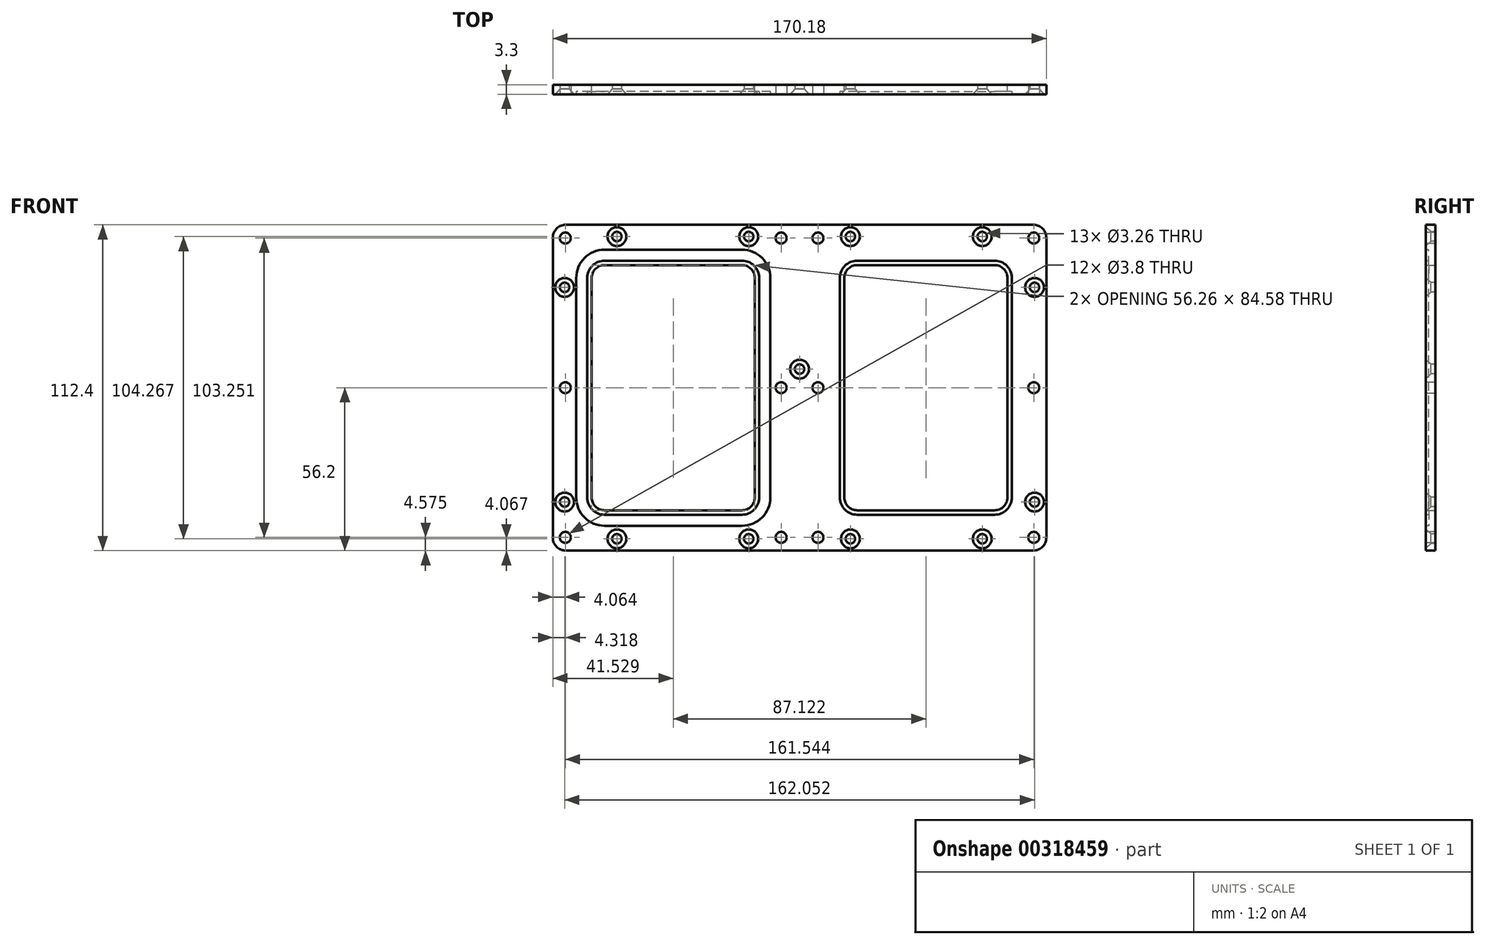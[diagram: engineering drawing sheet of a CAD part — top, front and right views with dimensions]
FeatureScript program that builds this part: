
annotation { "Feature Type Name" : "Feature", "Feature Type Description" : "" }
export const myFeature = defineFeature(function(context is Context, id is Id, definition is map)
    precondition{}
    {
        {
            var Q0;
            Q0=qCreatedBy(makeId("Front.planeOp"),FACE);
            var sketch = newSketch(context, id + "F0", { "sketchPlane" : qUnion([Q0])});
            skLineSegment(sketch, "E0.bottom", {"start": v(-80.64, -56.2) * mm, "end": v(80.65, -56.2) * mm});
            skLineSegment(sketch, "E0.top", {"start": v(-80.64, 56.2) * mm, "end": v(80.64, 56.2) * mm});
            skLineSegment(sketch, "E0.left", {"start": v(-85.1, -51.75) * mm, "end": v(-85.1, 51.75) * mm});
            skLineSegment(sketch, "E0.right", {"start": v(85.1, -51.75) * mm, "end": v(85.09, 51.75) * mm});
            skPoint(sketch, "E0.middle", {"position": v(0, 0) * mm});
            skPoint(sketch, "E1.visualSharp", {"position": v(-85.1, 56.2) * mm});
            skArc(sketch, "E1.filletArc", {"start": v(-80.65, 56.2) * mm, "mid": v(-83.79, 54.9) * mm, "end": v(-85.1, 51.75) * mm});
            skPoint(sketch, "E2.visualSharp", {"position": v(85.09, 56.2) * mm});
            skArc(sketch, "E2.filletArc", {"start": v(85.09, 51.75) * mm, "mid": v(83.79, 54.9) * mm, "end": v(80.64, 56.2) * mm});
            skPoint(sketch, "E3.visualSharp", {"position": v(85.1, -56.2) * mm});
            skArc(sketch, "E3.filletArc", {"start": v(80.65, -56.2) * mm, "mid": v(83.79, -54.9) * mm, "end": v(85.1, -51.75) * mm});
            skPoint(sketch, "E4.visualSharp", {"position": v(-85.1, -56.2) * mm});
            skArc(sketch, "E4.filletArc", {"start": v(-85.1, -51.75) * mm, "mid": v(-83.79, -54.9) * mm, "end": v(-80.64, -56.2) * mm});
            skLineSegment(sketch, "E5.bottom", {"start": v(-19.88, -42.3) * mm, "end": v(-67.25, -42.3) * mm});
            skLineSegment(sketch, "E5.top", {"start": v(-19.88, 42.3) * mm, "end": v(-67.25, 42.3) * mm});
            skLineSegment(sketch, "E5.left", {"start": v(-15.43, -37.85) * mm, "end": v(-15.43, 37.85) * mm});
            skLineSegment(sketch, "E5.right", {"start": v(-71.7, -37.85) * mm, "end": v(-71.7, 37.85) * mm});
            skPoint(sketch, "E5.middle", {"position": v(-43.56, 0) * mm});
            skPoint(sketch, "E6.visualSharp", {"position": v(-71.7, 42.3) * mm});
            skArc(sketch, "E6.filletArc", {"start": v(-67.25, 42.3) * mm, "mid": v(-70.39, 40.99) * mm, "end": v(-71.7, 37.85) * mm});
            skPoint(sketch, "E7.visualSharp", {"position": v(-15.43, 42.3) * mm});
            skArc(sketch, "E7.filletArc", {"start": v(-15.43, 37.85) * mm, "mid": v(-16.73, 40.99) * mm, "end": v(-19.88, 42.3) * mm});
            skPoint(sketch, "E8.visualSharp", {"position": v(-15.43, -42.3) * mm});
            skArc(sketch, "E8.filletArc", {"start": v(-19.88, -42.3) * mm, "mid": v(-16.73, -40.99) * mm, "end": v(-15.43, -37.85) * mm});
            skPoint(sketch, "E9.visualSharp", {"position": v(-71.7, -42.3) * mm});
            skArc(sketch, "E9.filletArc", {"start": v(-71.7, -37.85) * mm, "mid": v(-70.39, -40.99) * mm, "end": v(-67.25, -42.3) * mm});
            skArc(sketch, "E10.MirrorCS", {"start": v(67.25, 42.3) * mm, "mid": v(70.39, 40.99) * mm, "end": v(71.7, 37.85) * mm});
            skArc(sketch, "E11.MirrorCS", {"start": v(15.43, 37.85) * mm, "mid": v(16.73, 40.99) * mm, "end": v(19.88, 42.3) * mm});
            skArc(sketch, "E12.MirrorCS", {"start": v(19.88, -42.3) * mm, "mid": v(16.73, -40.99) * mm, "end": v(15.43, -37.85) * mm});
            skArc(sketch, "E13.MirrorCS", {"start": v(71.7, -37.85) * mm, "mid": v(70.39, -40.99) * mm, "end": v(67.25, -42.3) * mm});
            skPoint(sketch, "E14.MirrorP", {"position": v(43.56, 0) * mm});
            skPoint(sketch, "E15.MirrorP", {"position": v(15.43, -42.3) * mm});
            skLineSegment(sketch, "E16.MirrorCS", {"start": v(71.7, -37.85) * mm, "end": v(71.7, 37.85) * mm});
            skPoint(sketch, "E17.MirrorP", {"position": v(15.43, 42.3) * mm});
            skPoint(sketch, "E18.MirrorP", {"position": v(71.7, 42.3) * mm});
            skPoint(sketch, "E19.MirrorP", {"position": v(71.7, -42.3) * mm});
            skLineSegment(sketch, "E20.MirrorCS", {"start": v(15.43, -37.85) * mm, "end": v(15.43, 37.85) * mm});
            skLineSegment(sketch, "E21.MirrorCS", {"start": v(19.88, 42.3) * mm, "end": v(67.25, 42.3) * mm});
            skLineSegment(sketch, "E22.MirrorCS", {"start": v(19.88, -42.3) * mm, "end": v(67.25, -42.3) * mm});
            skSolve(sketch);
        }
        {
            var Q0;
            Q0=makeQuery(id+"F0.imprint","IMPRINT",FACE,{"disambiguationData":[TD([[makeQuery(id+"F0.imprint","IMPRINT",EDGE,{"derivedFrom":sQuery(id+"F0.wireOp",EDGE,"E0.bottom")}),1.0]])]});
            extrude(context, id + "F1", {"entities" : qUnion([Q0]), "depth" : 3.3 * mm});
        }
        {
            var Q0;
            Q0=makeQuery(id+"F1.opExtrude","CAP_FACE",FACE,{"disambiguationData":[OSD([sQuery(id+"F0.wireOp",EDGE,"E0.bottom"),sQuery(id+"F0.wireOp",EDGE,"E0.top"),sQuery(id+"F0.wireOp",EDGE,"E0.left"),sQuery(id+"F0.wireOp",EDGE,"E0.right"),sQuery(id+"F0.wireOp",EDGE,"E1.filletArc"),sQuery(id+"F0.wireOp",EDGE,"E2.filletArc"),sQuery(id+"F0.wireOp",EDGE,"E3.filletArc"),sQuery(id+"F0.wireOp",EDGE,"E4.filletArc"),sQuery(id+"F0.wireOp",EDGE,"E5.bottom"),sQuery(id+"F0.wireOp",EDGE,"E5.top"),sQuery(id+"F0.wireOp",EDGE,"E5.left"),sQuery(id+"F0.wireOp",EDGE,"E5.right"),sQuery(id+"F0.wireOp",EDGE,"E6.filletArc"),sQuery(id+"F0.wireOp",EDGE,"E7.filletArc"),sQuery(id+"F0.wireOp",EDGE,"E8.filletArc"),sQuery(id+"F0.wireOp",EDGE,"E9.filletArc"),sQuery(id+"F0.wireOp",EDGE,"E10.MirrorCS"),sQuery(id+"F0.wireOp",EDGE,"E11.MirrorCS"),sQuery(id+"F0.wireOp",EDGE,"E12.MirrorCS"),sQuery(id+"F0.wireOp",EDGE,"E13.MirrorCS"),sQuery(id+"F0.wireOp",EDGE,"E16.MirrorCS"),sQuery(id+"F0.wireOp",EDGE,"E20.MirrorCS"),sQuery(id+"F0.wireOp",EDGE,"E21.MirrorCS"),sQuery(id+"F0.wireOp",EDGE,"E22.MirrorCS")])],"isStart":false});
            var sketch = newSketch(context, id + "F2", { "sketchPlane" : qUnion([Q0])});
            skArc(sketch, "E23.0", {"start": v(-13.9, 37.85) * mm, "mid": v(-15.65, 42.07) * mm, "end": v(-19.88, 43.82) * mm});
            skLineSegment(sketch, "E23.1", {"start": v(-13.9, -37.85) * mm, "end": v(-13.9, 37.85) * mm});
            skLineSegment(sketch, "E23.2", {"start": v(-19.88, 43.82) * mm, "end": v(-67.25, 43.82) * mm});
            skArc(sketch, "E23.3", {"start": v(-19.88, -43.82) * mm, "mid": v(-15.65, -42.07) * mm, "end": v(-13.9, -37.85) * mm});
            skArc(sketch, "E23.4", {"start": v(-67.25, 43.81) * mm, "mid": v(-71.47, 42.07) * mm, "end": v(-73.22, 37.85) * mm});
            skLineSegment(sketch, "E23.5", {"start": v(-73.22, -37.85) * mm, "end": v(-73.22, 37.85) * mm});
            skArc(sketch, "E23.6", {"start": v(-73.22, -37.85) * mm, "mid": v(-71.47, -42.07) * mm, "end": v(-67.25, -43.81) * mm});
            skLineSegment(sketch, "E23.7", {"start": v(-19.88, -43.82) * mm, "end": v(-67.25, -43.81) * mm});
            skLineSegment(sketch, "E24.0", {"start": v(-19.88, 47.63) * mm, "end": v(-67.25, 47.63) * mm});
            skArc(sketch, "E24.1", {"start": v(-10.1, 37.85) * mm, "mid": v(-12.96, 44.76) * mm, "end": v(-19.88, 47.63) * mm});
            skArc(sketch, "E24.2", {"start": v(-67.25, 47.62) * mm, "mid": v(-74.16, 44.76) * mm, "end": v(-77.03, 37.85) * mm});
            skLineSegment(sketch, "E24.3", {"start": v(-10.1, -37.85) * mm, "end": v(-10.1, 37.85) * mm});
            skLineSegment(sketch, "E24.4", {"start": v(-77.03, -37.85) * mm, "end": v(-77.03, 37.85) * mm});
            skArc(sketch, "E24.5", {"start": v(-77.03, -37.85) * mm, "mid": v(-74.16, -44.76) * mm, "end": v(-67.25, -47.62) * mm});
            skLineSegment(sketch, "E24.6", {"start": v(-19.88, -47.63) * mm, "end": v(-67.25, -47.62) * mm});
            skArc(sketch, "E24.7", {"start": v(-19.88, -47.63) * mm, "mid": v(-12.96, -44.76) * mm, "end": v(-10.1, -37.85) * mm});
            skArc(sketch, "E25.MirrorCS", {"start": v(73.22, -37.85) * mm, "mid": v(71.47, -42.07) * mm, "end": v(67.25, -43.81) * mm});
            skLineSegment(sketch, "E26.MirrorCS", {"start": v(73.22, -37.85) * mm, "end": v(73.22, 37.85) * mm});
            skArc(sketch, "E27.MirrorCS", {"start": v(67.25, 43.81) * mm, "mid": v(71.47, 42.07) * mm, "end": v(73.22, 37.85) * mm});
            skArc(sketch, "E28.MirrorCS", {"start": v(19.88, -43.82) * mm, "mid": v(15.65, -42.07) * mm, "end": v(13.9, -37.85) * mm});
            skLineSegment(sketch, "E29.MirrorCS", {"start": v(19.88, 43.82) * mm, "end": v(67.25, 43.82) * mm});
            skLineSegment(sketch, "E30.MirrorCS", {"start": v(13.9, -37.85) * mm, "end": v(13.9, 37.85) * mm});
            skArc(sketch, "E31.MirrorCS", {"start": v(13.9, 37.85) * mm, "mid": v(15.65, 42.07) * mm, "end": v(19.88, 43.82) * mm});
            skArc(sketch, "E32.MirrorCS", {"start": v(19.88, -47.63) * mm, "mid": v(12.96, -44.76) * mm, "end": v(10.1, -37.85) * mm});
            skLineSegment(sketch, "E33.MirrorCS", {"start": v(19.88, -47.63) * mm, "end": v(67.25, -47.62) * mm});
            skLineSegment(sketch, "E34.MirrorCS", {"start": v(19.88, -43.82) * mm, "end": v(67.25, -43.81) * mm});
            skArc(sketch, "E35.MirrorCS", {"start": v(77.03, -37.85) * mm, "mid": v(74.16, -44.76) * mm, "end": v(67.25, -47.62) * mm});
            skLineSegment(sketch, "E36.MirrorCS", {"start": v(77.03, -37.85) * mm, "end": v(77.03, 37.85) * mm});
            skLineSegment(sketch, "E37.MirrorCS", {"start": v(10.1, -37.85) * mm, "end": v(10.1, 37.85) * mm});
            skArc(sketch, "E38.MirrorCS", {"start": v(67.25, 47.62) * mm, "mid": v(74.16, 44.76) * mm, "end": v(77.03, 37.85) * mm});
            skArc(sketch, "E39.MirrorCS", {"start": v(10.1, 37.85) * mm, "mid": v(12.96, 44.76) * mm, "end": v(19.88, 47.63) * mm});
            skLineSegment(sketch, "E40.MirrorCS", {"start": v(19.88, 47.63) * mm, "end": v(67.25, 47.63) * mm});
            skSolve(sketch);
        }
        {
            var Q0;
            Q0=makeQuery(id+"F2.imprint","IMPRINT",FACE,{"disambiguationData":[TD([[makeQuery(id+"F2.imprint","IMPRINT",EDGE,{"derivedFrom":sQuery(id+"F2.wireOp",EDGE,"E23.0")}),-1.0]])]});
            var Q1;
            Q1=makeQuery(id+"F2.imprint","IMPRINT",FACE,{"disambiguationData":[TD([[makeQuery(id+"F2.imprint","IMPRINT",EDGE,{"derivedFrom":sQuery(id+"F2.wireOp",EDGE,"E25.MirrorCS")}),1.0]])]});
            extrude(context, id + "F3", {"entities" : qUnion([Q0, Q1]), "operationType" : NewBodyOperationType.REMOVE, "oppositeDirection" : true, "depth" : 1.02 * mm});
        }
        {
            var Q0;
            Q0=makeQuery(id+"F1.opExtrude","CAP_FACE",FACE,{"disambiguationData":[OSD([sQuery(id+"F0.wireOp",EDGE,"E0.bottom"),sQuery(id+"F0.wireOp",EDGE,"E0.top"),sQuery(id+"F0.wireOp",EDGE,"E0.left"),sQuery(id+"F0.wireOp",EDGE,"E0.right"),sQuery(id+"F0.wireOp",EDGE,"E1.filletArc"),sQuery(id+"F0.wireOp",EDGE,"E2.filletArc"),sQuery(id+"F0.wireOp",EDGE,"E3.filletArc"),sQuery(id+"F0.wireOp",EDGE,"E4.filletArc"),sQuery(id+"F0.wireOp",EDGE,"E5.bottom"),sQuery(id+"F0.wireOp",EDGE,"E5.top"),sQuery(id+"F0.wireOp",EDGE,"E5.left"),sQuery(id+"F0.wireOp",EDGE,"E5.right"),sQuery(id+"F0.wireOp",EDGE,"E6.filletArc"),sQuery(id+"F0.wireOp",EDGE,"E7.filletArc"),sQuery(id+"F0.wireOp",EDGE,"E8.filletArc"),sQuery(id+"F0.wireOp",EDGE,"E9.filletArc"),sQuery(id+"F0.wireOp",EDGE,"E10.MirrorCS"),sQuery(id+"F0.wireOp",EDGE,"E11.MirrorCS"),sQuery(id+"F0.wireOp",EDGE,"E12.MirrorCS"),sQuery(id+"F0.wireOp",EDGE,"E13.MirrorCS"),sQuery(id+"F0.wireOp",EDGE,"E16.MirrorCS"),sQuery(id+"F0.wireOp",EDGE,"E20.MirrorCS"),sQuery(id+"F0.wireOp",EDGE,"E21.MirrorCS"),sQuery(id+"F0.wireOp",EDGE,"E22.MirrorCS")])],"isStart":true});
            var Q1;
            {var subQ0=sQuery(id+"F0.wireOp",EDGE,"E0.left");var subQ1=sQuery(id+"F0.wireOp",EDGE,"E0.top");var subQ2=sQuery(id+"F0.wireOp",EDGE,"E0.right");var subQ3=sQuery(id+"F0.wireOp",EDGE,"E0.bottom");var subQ4=sQuery(id+"F0.wireOp",EDGE,"E1.filletArc");var subQ5=sQuery(id+"F0.wireOp",EDGE,"E2.filletArc");var subQ6=sQuery(id+"F0.wireOp",EDGE,"E3.filletArc");var subQ7=sQuery(id+"F0.wireOp",EDGE,"E4.filletArc");Q1=makeQuery(id+"F3.boolean.opBoolean","SPLIT",FACE,{"disambiguationData":[TD([makeQuery(id+"F1.opExtrude","SWEPT_FACE",FACE,{"disambiguationData":[OSD([subQ3])]})])],"derivedFrom":makeQuery(id+"F1.opExtrude","CAP_FACE",FACE,{"disambiguationData":[OSD([subQ3,subQ1,subQ0,subQ2,subQ4,subQ5,subQ6,subQ7,sQuery(id+"F0.wireOp",EDGE,"E5.bottom"),sQuery(id+"F0.wireOp",EDGE,"E5.top"),sQuery(id+"F0.wireOp",EDGE,"E5.left"),sQuery(id+"F0.wireOp",EDGE,"E5.right"),sQuery(id+"F0.wireOp",EDGE,"E6.filletArc"),sQuery(id+"F0.wireOp",EDGE,"E7.filletArc"),sQuery(id+"F0.wireOp",EDGE,"E8.filletArc"),sQuery(id+"F0.wireOp",EDGE,"E9.filletArc"),sQuery(id+"F0.wireOp",EDGE,"E10.MirrorCS"),sQuery(id+"F0.wireOp",EDGE,"E11.MirrorCS"),sQuery(id+"F0.wireOp",EDGE,"E12.MirrorCS"),sQuery(id+"F0.wireOp",EDGE,"E13.MirrorCS"),sQuery(id+"F0.wireOp",EDGE,"E16.MirrorCS"),sQuery(id+"F0.wireOp",EDGE,"E20.MirrorCS"),sQuery(id+"F0.wireOp",EDGE,"E21.MirrorCS"),sQuery(id+"F0.wireOp",EDGE,"E22.MirrorCS")])],"isStart":false})});}
            cPlane(context, id + "F4", {"entities" : qUnion([Q0, Q1]), "cplaneType" : CPlaneType.MID_PLANE, "offset" : 25.4 * mm, "width" : 152.4 * mm, "height" : 152.4 * mm});
        }
        {
            var Q0;
            {var subQ0=sQuery(id+"F0.wireOp",EDGE,"E0.left");var subQ1=sQuery(id+"F0.wireOp",EDGE,"E0.top");var subQ2=sQuery(id+"F0.wireOp",EDGE,"E0.right");var subQ3=sQuery(id+"F0.wireOp",EDGE,"E0.bottom");var subQ4=sQuery(id+"F0.wireOp",EDGE,"E1.filletArc");var subQ5=sQuery(id+"F0.wireOp",EDGE,"E2.filletArc");var subQ6=sQuery(id+"F0.wireOp",EDGE,"E3.filletArc");var subQ7=sQuery(id+"F0.wireOp",EDGE,"E4.filletArc");Q0=makeQuery(id+"F3.boolean.opBoolean","SPLIT",FACE,{"disambiguationData":[TD([makeQuery(id+"F1.opExtrude","SWEPT_FACE",FACE,{"disambiguationData":[OSD([subQ3])]})])],"derivedFrom":makeQuery(id+"F1.opExtrude","CAP_FACE",FACE,{"disambiguationData":[OSD([subQ3,subQ1,subQ0,subQ2,subQ4,subQ5,subQ6,subQ7,sQuery(id+"F0.wireOp",EDGE,"E5.bottom"),sQuery(id+"F0.wireOp",EDGE,"E5.top"),sQuery(id+"F0.wireOp",EDGE,"E5.left"),sQuery(id+"F0.wireOp",EDGE,"E5.right"),sQuery(id+"F0.wireOp",EDGE,"E6.filletArc"),sQuery(id+"F0.wireOp",EDGE,"E7.filletArc"),sQuery(id+"F0.wireOp",EDGE,"E8.filletArc"),sQuery(id+"F0.wireOp",EDGE,"E9.filletArc"),sQuery(id+"F0.wireOp",EDGE,"E10.MirrorCS"),sQuery(id+"F0.wireOp",EDGE,"E11.MirrorCS"),sQuery(id+"F0.wireOp",EDGE,"E12.MirrorCS"),sQuery(id+"F0.wireOp",EDGE,"E13.MirrorCS"),sQuery(id+"F0.wireOp",EDGE,"E16.MirrorCS"),sQuery(id+"F0.wireOp",EDGE,"E20.MirrorCS"),sQuery(id+"F0.wireOp",EDGE,"E21.MirrorCS"),sQuery(id+"F0.wireOp",EDGE,"E22.MirrorCS")])],"isStart":false})});}
            var sketch = newSketch(context, id + "F5", { "sketchPlane" : qUnion([Q0])});
            skPoint(sketch, "E41", {"position": v(0, 6.41) * mm});
            skPoint(sketch, "E42", {"position": v(-63, 52.13) * mm});
            skPoint(sketch, "E43", {"position": v(-17.53, 52.13) * mm});
            skPoint(sketch, "E44", {"position": v(-81.03, -39.43) * mm});
            skPoint(sketch, "E45", {"position": v(-81.03, 34.6) * mm});
            skPoint(sketch, "E46", {"position": v(-63, -52.13) * mm});
            skPoint(sketch, "E47", {"position": v(-17.53, -52.13) * mm});
            skPoint(sketch, "E48.MirrorP", {"position": v(63, 52.13) * mm});
            skPoint(sketch, "E49.MirrorP", {"position": v(17.53, 52.13) * mm});
            skPoint(sketch, "E50.MirrorP", {"position": v(17.53, -52.13) * mm});
            skPoint(sketch, "E51.MirrorP", {"position": v(81.03, -39.43) * mm});
            skPoint(sketch, "E52.MirrorP", {"position": v(81.03, 34.6) * mm});
            skPoint(sketch, "E53.MirrorP", {"position": v(63, -52.13) * mm});
            skSolve(sketch);
        }
        {
            var Q0;
            Q0=sQuery(id+"F5.wireOp",VERTEX,"E45");
            var Q1;
            Q1=sQuery(id+"F5.wireOp",VERTEX,"E44");
            var Q2;
            Q2=sQuery(id+"F5.wireOp",VERTEX,"E42");
            var Q3;
            Q3=sQuery(id+"F5.wireOp",VERTEX,"E43");
            var Q4;
            Q4=sQuery(id+"F5.wireOp",VERTEX,"E41");
            var Q5;
            Q5=sQuery(id+"F5.wireOp",VERTEX,"E46");
            var Q6;
            Q6=sQuery(id+"F5.wireOp",VERTEX,"E47");
            var Q7;
            Q7=sQuery(id+"F5.wireOp",VERTEX,"E50.MirrorP");
            var Q8;
            Q8=sQuery(id+"F5.wireOp",VERTEX,"E53.MirrorP");
            var Q9;
            Q9=sQuery(id+"F5.wireOp",VERTEX,"E51.MirrorP");
            var Q10;
            Q10=sQuery(id+"F5.wireOp",VERTEX,"E52.MirrorP");
            var Q11;
            Q11=sQuery(id+"F5.wireOp",VERTEX,"E48.MirrorP");
            var Q12;
            Q12=sQuery(id+"F5.wireOp",VERTEX,"E49.MirrorP");
            var Q13;
            Q13=makeQuery(id+"F1.opExtrude","SWEPT_BODY",BODY,{"disambiguationData":[OSD([sQuery(id+"F0.wireOp",EDGE,"E0.bottom"),sQuery(id+"F0.wireOp",EDGE,"E0.top"),sQuery(id+"F0.wireOp",EDGE,"E0.left"),sQuery(id+"F0.wireOp",EDGE,"E0.right"),sQuery(id+"F0.wireOp",EDGE,"E1.filletArc"),sQuery(id+"F0.wireOp",EDGE,"E2.filletArc"),sQuery(id+"F0.wireOp",EDGE,"E3.filletArc"),sQuery(id+"F0.wireOp",EDGE,"E4.filletArc"),sQuery(id+"F0.wireOp",EDGE,"E5.bottom"),sQuery(id+"F0.wireOp",EDGE,"E5.top"),sQuery(id+"F0.wireOp",EDGE,"E5.left"),sQuery(id+"F0.wireOp",EDGE,"E5.right"),sQuery(id+"F0.wireOp",EDGE,"E6.filletArc"),sQuery(id+"F0.wireOp",EDGE,"E7.filletArc"),sQuery(id+"F0.wireOp",EDGE,"E8.filletArc"),sQuery(id+"F0.wireOp",EDGE,"E9.filletArc"),sQuery(id+"F0.wireOp",EDGE,"E10.MirrorCS"),sQuery(id+"F0.wireOp",EDGE,"E11.MirrorCS"),sQuery(id+"F0.wireOp",EDGE,"E12.MirrorCS"),sQuery(id+"F0.wireOp",EDGE,"E13.MirrorCS"),sQuery(id+"F0.wireOp",EDGE,"E16.MirrorCS"),sQuery(id+"F0.wireOp",EDGE,"E20.MirrorCS"),sQuery(id+"F0.wireOp",EDGE,"E21.MirrorCS"),sQuery(id+"F0.wireOp",EDGE,"E22.MirrorCS")])]});
            hole(context, id + "F6", {"style" : HoleStyle.C_SINK, "endStyle" : HoleEndStyle.THROUGH, "standardTappedOrClearance" : lookupTablePath({ "standard" : "ANSI", "fit" : "Normal (ASME)", "size" : "#4", "type" : "Clearance" }), "standardBlindInLast" : lookupTablePath({ "fit" : "Free", "standard" : "ANSI", "size" : "#4", "type" : "Clearance" }), "holeDiameter" : 3.26 * mm, "cSinkDiameter" : 6.48 * mm, "cSinkAngle" : 82 * degree, "tappedDepth" : 6.35 * mm, "tapClearance" : 3, "locations" : qUnion([Q0, Q1, Q2, Q3, Q4, Q5, Q6, Q7, Q8, Q9, Q10, Q11, Q12]), "scope" : qUnion([Q13])});
        }
        {
            var Q0;
            {var subQ0=sQuery(id+"F0.wireOp",EDGE,"E0.left");var subQ1=sQuery(id+"F0.wireOp",EDGE,"E0.top");var subQ2=sQuery(id+"F0.wireOp",EDGE,"E0.right");var subQ3=sQuery(id+"F0.wireOp",EDGE,"E0.bottom");var subQ4=sQuery(id+"F0.wireOp",EDGE,"E1.filletArc");var subQ5=sQuery(id+"F0.wireOp",EDGE,"E2.filletArc");var subQ6=sQuery(id+"F0.wireOp",EDGE,"E3.filletArc");var subQ7=sQuery(id+"F0.wireOp",EDGE,"E4.filletArc");Q0=makeQuery(id+"F3.boolean.opBoolean","SPLIT",FACE,{"disambiguationData":[TD([makeQuery(id+"F1.opExtrude","SWEPT_FACE",FACE,{"disambiguationData":[OSD([subQ3])]})])],"derivedFrom":makeQuery(id+"F1.opExtrude","CAP_FACE",FACE,{"disambiguationData":[OSD([subQ3,subQ1,subQ0,subQ2,subQ4,subQ5,subQ6,subQ7,sQuery(id+"F0.wireOp",EDGE,"E5.bottom"),sQuery(id+"F0.wireOp",EDGE,"E5.top"),sQuery(id+"F0.wireOp",EDGE,"E5.left"),sQuery(id+"F0.wireOp",EDGE,"E5.right"),sQuery(id+"F0.wireOp",EDGE,"E6.filletArc"),sQuery(id+"F0.wireOp",EDGE,"E7.filletArc"),sQuery(id+"F0.wireOp",EDGE,"E8.filletArc"),sQuery(id+"F0.wireOp",EDGE,"E9.filletArc"),sQuery(id+"F0.wireOp",EDGE,"E10.MirrorCS"),sQuery(id+"F0.wireOp",EDGE,"E11.MirrorCS"),sQuery(id+"F0.wireOp",EDGE,"E12.MirrorCS"),sQuery(id+"F0.wireOp",EDGE,"E13.MirrorCS"),sQuery(id+"F0.wireOp",EDGE,"E16.MirrorCS"),sQuery(id+"F0.wireOp",EDGE,"E20.MirrorCS"),sQuery(id+"F0.wireOp",EDGE,"E21.MirrorCS"),sQuery(id+"F0.wireOp",EDGE,"E22.MirrorCS")])],"isStart":false})});}
            var sketch = newSketch(context, id + "F7", { "sketchPlane" : qUnion([Q0])});
            skPoint(sketch, "E54", {"position": v(-80.77, 51.63) * mm});
            skPoint(sketch, "E55", {"position": v(-80.77, 0) * mm});
            skPoint(sketch, "E56", {"position": v(-80.77, -51.63) * mm});
            skPoint(sketch, "E57", {"position": v(-6.35, -51.63) * mm});
            skPoint(sketch, "E58", {"position": v(-6.35, 0) * mm});
            skPoint(sketch, "E59", {"position": v(-6.35, 51.63) * mm});
            skPoint(sketch, "E60.MirrorP", {"position": v(6.35, -51.63) * mm});
            skPoint(sketch, "E61.MirrorP", {"position": v(80.77, 51.63) * mm});
            skPoint(sketch, "E62.MirrorP", {"position": v(6.35, 51.63) * mm});
            skPoint(sketch, "E63.MirrorP", {"position": v(6.35, 0) * mm});
            skPoint(sketch, "E64.MirrorP", {"position": v(80.77, -51.63) * mm});
            skPoint(sketch, "E65.MirrorP", {"position": v(80.77, 0) * mm});
            skSolve(sketch);
        }
        {
            var Q0;
            Q0=sQuery(id+"F7.wireOp",VERTEX,"E54");
            var Q1;
            Q1=sQuery(id+"F7.wireOp",VERTEX,"E55");
            var Q2;
            Q2=sQuery(id+"F7.wireOp",VERTEX,"E56");
            var Q3;
            Q3=sQuery(id+"F7.wireOp",VERTEX,"E57");
            var Q4;
            Q4=sQuery(id+"F7.wireOp",VERTEX,"E58");
            var Q5;
            Q5=sQuery(id+"F7.wireOp",VERTEX,"E63.MirrorP");
            var Q6;
            Q6=sQuery(id+"F7.wireOp",VERTEX,"E59");
            var Q7;
            Q7=sQuery(id+"F7.wireOp",VERTEX,"E62.MirrorP");
            var Q8;
            Q8=sQuery(id+"F7.wireOp",VERTEX,"E60.MirrorP");
            var Q9;
            Q9=sQuery(id+"F7.wireOp",VERTEX,"E64.MirrorP");
            var Q10;
            Q10=sQuery(id+"F7.wireOp",VERTEX,"E61.MirrorP");
            var Q11;
            Q11=sQuery(id+"F7.wireOp",VERTEX,"E65.MirrorP");
            var Q12;
            Q12=makeQuery(id+"F1.opExtrude","SWEPT_BODY",BODY,{"disambiguationData":[OSD([sQuery(id+"F0.wireOp",EDGE,"E0.bottom"),sQuery(id+"F0.wireOp",EDGE,"E0.top"),sQuery(id+"F0.wireOp",EDGE,"E0.left"),sQuery(id+"F0.wireOp",EDGE,"E0.right"),sQuery(id+"F0.wireOp",EDGE,"E1.filletArc"),sQuery(id+"F0.wireOp",EDGE,"E2.filletArc"),sQuery(id+"F0.wireOp",EDGE,"E3.filletArc"),sQuery(id+"F0.wireOp",EDGE,"E4.filletArc"),sQuery(id+"F0.wireOp",EDGE,"E5.bottom"),sQuery(id+"F0.wireOp",EDGE,"E5.top"),sQuery(id+"F0.wireOp",EDGE,"E5.left"),sQuery(id+"F0.wireOp",EDGE,"E5.right"),sQuery(id+"F0.wireOp",EDGE,"E6.filletArc"),sQuery(id+"F0.wireOp",EDGE,"E7.filletArc"),sQuery(id+"F0.wireOp",EDGE,"E8.filletArc"),sQuery(id+"F0.wireOp",EDGE,"E9.filletArc"),sQuery(id+"F0.wireOp",EDGE,"E10.MirrorCS"),sQuery(id+"F0.wireOp",EDGE,"E11.MirrorCS"),sQuery(id+"F0.wireOp",EDGE,"E12.MirrorCS"),sQuery(id+"F0.wireOp",EDGE,"E13.MirrorCS"),sQuery(id+"F0.wireOp",EDGE,"E16.MirrorCS"),sQuery(id+"F0.wireOp",EDGE,"E20.MirrorCS"),sQuery(id+"F0.wireOp",EDGE,"E21.MirrorCS"),sQuery(id+"F0.wireOp",EDGE,"E22.MirrorCS")])]});
            hole(context, id + "F8", {"style" : HoleStyle.SIMPLE, "endStyle" : HoleEndStyle.THROUGH, "standardTappedOrClearance" : lookupTablePath({ "standard" : "ANSI", "fit" : "Normal (ASME)", "size" : "#6", "type" : "Clearance" }), "standardBlindInLast" : lookupTablePath({ "fit" : "Free", "standard" : "ANSI", "size" : "#6", "type" : "Clearance" }), "holeDiameter" : 3.8 * mm, "tappedDepth" : 6.35 * mm, "tapClearance" : 3, "locations" : qUnion([Q0, Q1, Q2, Q3, Q4, Q5, Q6, Q7, Q8, Q9, Q10, Q11]), "scope" : qUnion([Q12])});
        }
    });
